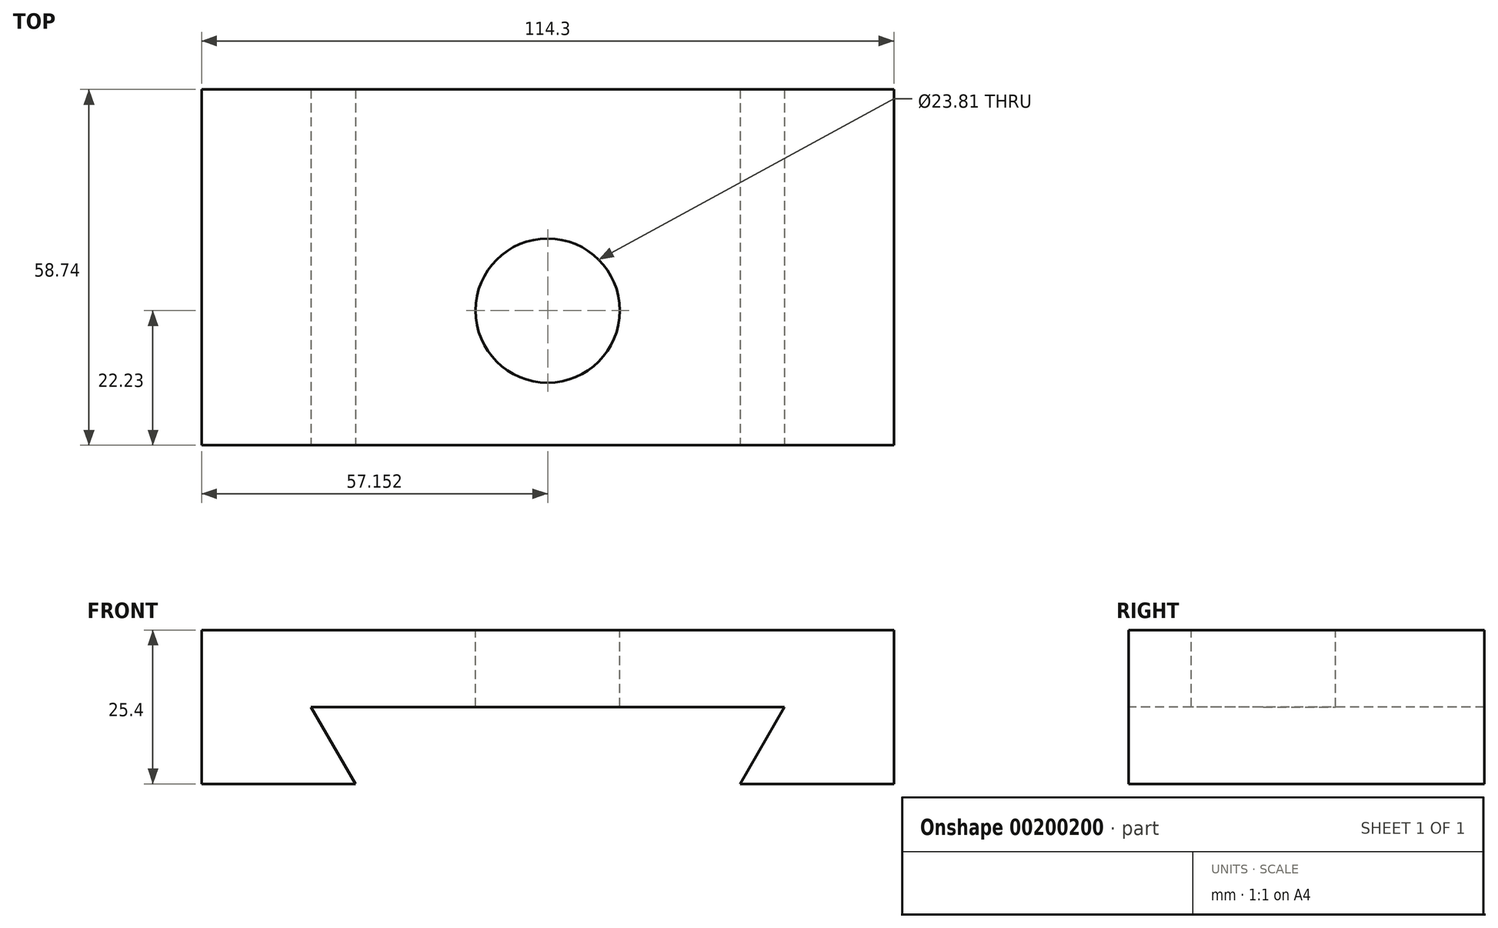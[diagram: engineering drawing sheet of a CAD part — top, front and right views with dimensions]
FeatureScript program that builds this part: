
annotation { "Feature Type Name" : "Feature", "Feature Type Description" : "" }
export const myFeature = defineFeature(function(context is Context, id is Id, definition is map)
    precondition{}
    {
        {
            var Q0;
            Q0=qCreatedBy(makeId("Top.planeOp"),FACE);
            var sketch = newSketch(context, id + "F0", { "sketchPlane" : qUnion([Q0])});
            skLineSegment(sketch, "E0.bottom", {"start": v(-61.47, 35.1) * mm, "end": v(52.83, 35.1) * mm});
            skLineSegment(sketch, "E0.top", {"start": v(-61.47, -23.65) * mm, "end": v(52.83, -23.65) * mm});
            skLineSegment(sketch, "E0.left", {"start": v(-61.47, 35.1) * mm, "end": v(-61.47, -23.65) * mm});
            skLineSegment(sketch, "E0.right", {"start": v(52.83, 35.1) * mm, "end": v(52.83, -23.65) * mm});
            skSolve(sketch);
        }
        {
            var Q0;
            Q0=makeQuery(id+"F0.imprint","IMPRINT",FACE,{"disambiguationData":[TD([[makeQuery(id+"F0.imprint","IMPRINT",EDGE,{"derivedFrom":sQuery(id+"F0.wireOp",EDGE,"E0.bottom")}),-1.0]])]});
            extrude(context, id + "F1", {"entities" : qUnion([Q0]), "oppositeDirection" : true, "depth" : 25.4 * mm});
        }
        {
            var Q0;
            Q0=makeQuery(id+"F1.opExtrude","SWEPT_FACE",FACE,{"disambiguationData":[OSD([sQuery(id+"F0.wireOp",EDGE,"E0.top")])]});
            var sketch = newSketch(context, id + "F2", { "sketchPlane" : qUnion([Q0])});
            skLineSegment(sketch, "E1.bottom", {"start": v(-36.07, -25.4) * mm, "end": v(27.43, -25.4) * mm});
            skLineSegment(sketch, "E1.top", {"start": v(-43.4, -12.7) * mm, "end": v(34.76, -12.7) * mm});
            skLineSegment(sketch, "E2", {"start": v(-43.4, -12.7) * mm, "end": v(-36.07, -25.4) * mm});
            skLineSegment(sketch, "E3", {"start": v(34.76, -12.7) * mm, "end": v(27.43, -25.4) * mm});
            skSolve(sketch);
        }
        {
            var Q0;
            Q0=makeQuery(id+"F2.imprint","IMPRINT",FACE,{"disambiguationData":[TD([[makeQuery(id+"F2.imprint","IMPRINT",EDGE,{"derivedFrom":sQuery(id+"F2.wireOp",EDGE,"E1.bottom")}),1.0]])]});
            extrude(context, id + "F3", {"entities" : qUnion([Q0]), "operationType" : NewBodyOperationType.REMOVE, "oppositeDirection" : true, "depth" : 70.36 * mm});
        }
        {
            var Q0;
            Q0=makeQuery(id+"F1.opExtrude","CAP_FACE",FACE,{"disambiguationData":[OSD([sQuery(id+"F0.wireOp",EDGE,"E0.bottom"),sQuery(id+"F0.wireOp",EDGE,"E0.top"),sQuery(id+"F0.wireOp",EDGE,"E0.left"),sQuery(id+"F0.wireOp",EDGE,"E0.right")])],"isStart":true});
            var sketch = newSketch(context, id + "F4", { "sketchPlane" : qUnion([Q0])});
            skCircle(sketch, "E4", {"center": v(-4.32, -1.42) * mm, "radius": 11.9 * mm});
            skSolve(sketch);
        }
        {
            var Q0;
            Q0=makeQuery(id+"F4.imprint","IMPRINT",FACE,{"disambiguationData":[TD([[makeQuery(id+"F4.imprint","IMPRINT",EDGE,{"derivedFrom":sQuery(id+"F4.wireOp",EDGE,"E4")}),1.0]])]});
            extrude(context, id + "F5", {"entities" : qUnion([Q0]), "operationType" : NewBodyOperationType.REMOVE, "oppositeDirection" : true, "depth" : 24.9 * mm});
        }
    });
